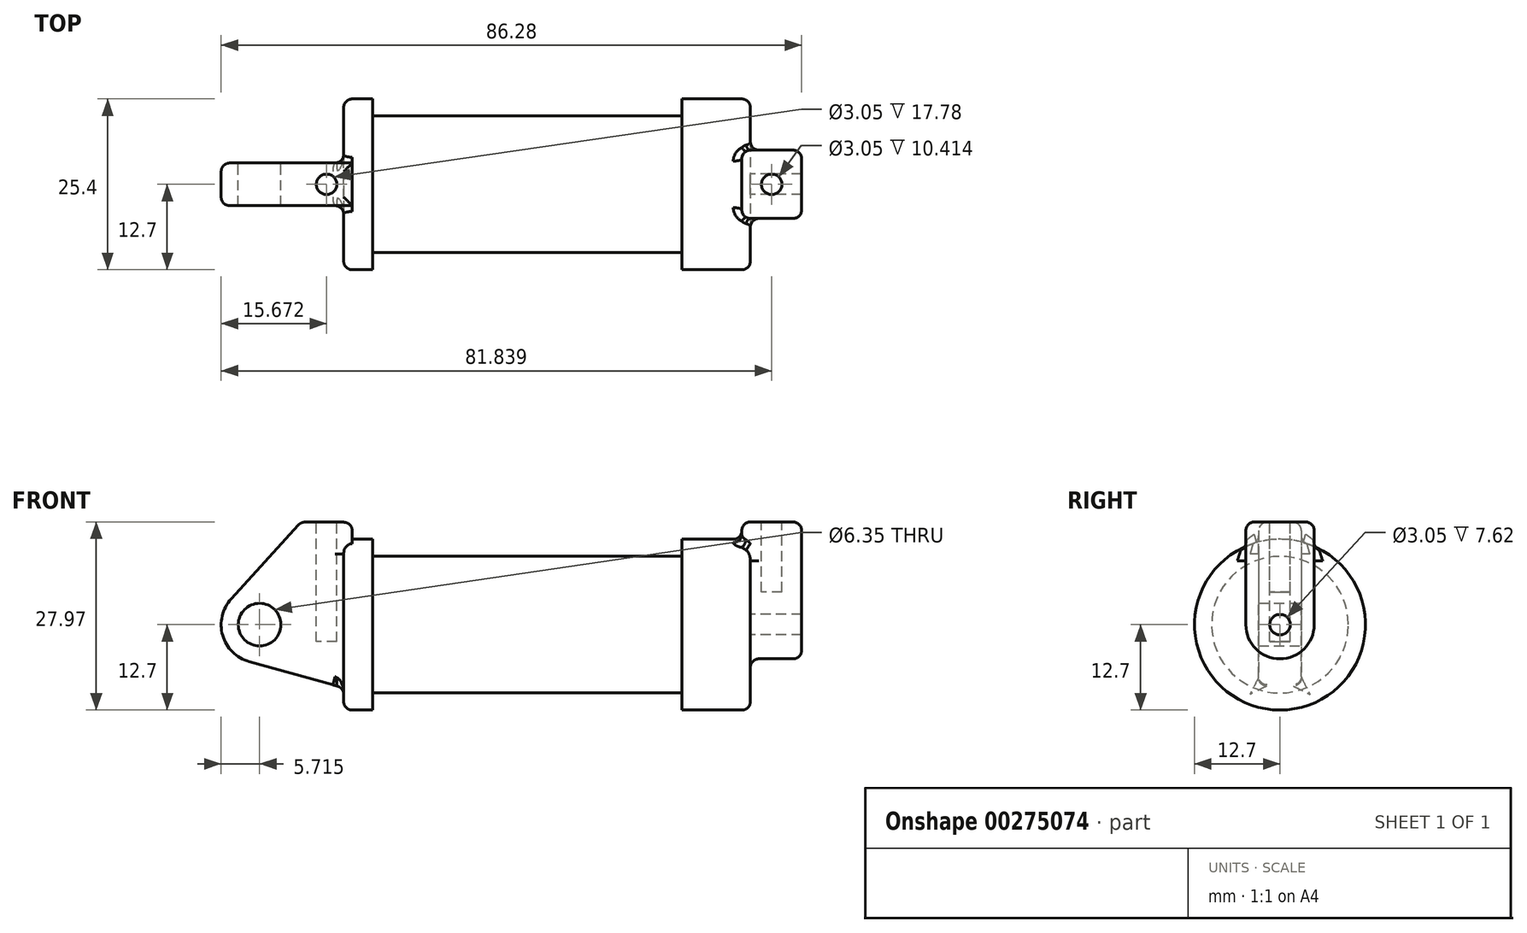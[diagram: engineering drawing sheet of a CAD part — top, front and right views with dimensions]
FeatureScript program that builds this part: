
annotation { "Feature Type Name" : "Feature", "Feature Type Description" : "" }
export const myFeature = defineFeature(function(context is Context, id is Id, definition is map)
    precondition{}
    {
        {
            var Q0;
            Q0=qCreatedBy(makeId("Front.planeOp"),FACE);
            var sketch = newSketch(context, id + "F0", { "sketchPlane" : qUnion([Q0])});
            skLineSegment(sketch, "E0", {"start": v(0, 0) * mm, "end": v(0, 12.7) * mm});
            skLineSegment(sketch, "E1", {"start": v(0, 12.7) * mm, "end": v(10.16, 12.7) * mm});
            skLineSegment(sketch, "E2", {"start": v(10.16, 12.7) * mm, "end": v(10.16, 10.16) * mm});
            skLineSegment(sketch, "E3", {"start": v(10.16, 10.16) * mm, "end": v(56.13, 10.16) * mm});
            skLineSegment(sketch, "E4", {"start": v(56.13, 10.16) * mm, "end": v(56.13, 12.7) * mm});
            skLineSegment(sketch, "E5", {"start": v(56.13, 12.7) * mm, "end": v(66.3, 12.7) * mm});
            skLineSegment(sketch, "E6", {"start": v(66.3, 12.7) * mm, "end": v(66.3, 0) * mm});
            skLineSegment(sketch, "E7", {"start": v(66.3, 0) * mm, "end": v(0, 0) * mm});
            skLineSegment(sketch, "E8", {"start": v(5.84, 15.24) * mm, "end": v(-0.5, 15.24) * mm});
            skLineSegment(sketch, "E9", {"start": v(-0.5, 15.24) * mm, "end": v(-10.88, 3.85) * mm});
            skLineSegment(sketch, "E10", {"start": v(0, 0) * mm, "end": v(-6.65, 0) * mm});
            skCircle(sketch, "E11", {"center": v(-6.65, 0) * mm, "radius": 5.72 * mm});
            skCircle(sketch, "E12", {"center": v(-6.65, 0) * mm, "radius": 3.18 * mm});
            skLineSegment(sketch, "E13", {"start": v(5.84, 15.24) * mm, "end": v(5.84, -9.4) * mm});
            skLineSegment(sketch, "E14", {"start": v(5.84, -9.4) * mm, "end": v(-8.18, -5.5) * mm});
            skSolve(sketch);
        }
        {
            var Q0;
            {var subQ0=sQuery(id+"F0.wireOp",EDGE,"E2");Q0=makeQuery(id+"F0.imprint","IMPRINT",FACE,{"disambiguationData":[TD([[makeQuery(id+"F0.imprint","IMPRINT",EDGE,{"derivedFrom":subQ0}),-1.0]])]});}
            var Q1;
            Q1=sQuery(id+"F0.wireOp",EDGE,"E7");
            revolve(context, id + "F1", {"entities" : qUnion([Q0]), "axis" : qUnion([Q1]), "revolveType" : RevolveType.FULL});
        }
        {
            var Q0;
            {var subQ3=sQuery(id+"F0.wireOp",EDGE,"E0");Q0=makeQuery(id+"F0.imprint","IMPRINT",FACE,{"disambiguationData":[TD([[makeQuery(id+"F0.imprint","IMPRINT",EDGE,{"derivedFrom":subQ3}),1.0]])]});}
            var Q1;
            {var subQ0=sQuery(id+"F0.wireOp",EDGE,"E0");Q1=makeQuery(id+"F0.imprint","IMPRINT",FACE,{"disambiguationData":[TD([[makeQuery(id+"F0.imprint","IMPRINT",EDGE,{"derivedFrom":subQ0}),-1.0]])]});}
            var Q2;
            {var subQ4=sQuery(id+"F0.wireOp",EDGE,"E12");Q2=makeQuery(id+"F0.imprint","IMPRINT",FACE,{"disambiguationData":[TD([[makeQuery(id+"F0.imprint","IMPRINT",EDGE,{"derivedFrom":subQ4}),-1.0]])]});}
            var Q3;
            {var subQ0=sQuery(id+"F0.wireOp",EDGE,"E14");Q3=makeQuery(id+"F0.imprint","IMPRINT",FACE,{"disambiguationData":[TD([[makeQuery(id+"F0.imprint","IMPRINT",EDGE,{"derivedFrom":subQ0}),-1.0]])]});}
            extrude(context, id + "F2", {"entities" : qUnion([Q0, Q1, Q2, Q3]), "operationType" : NewBodyOperationType.ADD, "endBound" : BoundingType.SYMMETRIC, "depth" : 6.35 * mm});
        }
        {
            var Q0;
            Q0=makeQuery(id+"F2.opExtrude","SWEPT_FACE",FACE,{"disambiguationData":[OSD([sQuery(id+"F0.wireOp",EDGE,"E13")])]});
            extrude(context, id + "F3", {"entities" : qUnion([Q0]), "operationType" : NewBodyOperationType.ADD, "depth" : 1.27 * mm});
        }
        {
            var Q0;
            Q0=makeQuery(id+"F1.opRevolve","SWEPT_FACE",FACE,{"disambiguationData":[OSD([sQuery(id+"F0.wireOp",EDGE,"E6")])]});
            var sketch = newSketch(context, id + "F4", { "sketchPlane" : qUnion([Q0])});
            skCircle(sketch, "E15", {"center": v(0, 0) * mm, "radius": 1.52 * mm});
            skCircle(sketch, "E16", {"center": v(0, 0) * mm, "radius": 5.08 * mm});
            skLineSegment(sketch, "E17", {"start": v(5.08, 0) * mm, "end": v(5.08, 15.27) * mm});
            skLineSegment(sketch, "E18", {"start": v(-5.08, 0) * mm, "end": v(-5.08, 15.27) * mm});
            skLineSegment(sketch, "E19", {"start": v(-5.08, 15.27) * mm, "end": v(5.08, 15.27) * mm});
            skSolve(sketch);
        }
        {
            var Q0;
            Q0=makeQuery(id+"F4.imprint","IMPRINT",FACE,{"disambiguationData":[TD([[makeQuery(id+"F4.imprint","IMPRINT",EDGE,{"derivedFrom":sQuery(id+"F4.wireOp",EDGE,"E15")}),-1.0]])]});
            var Q1;
            {var subQ0=sQuery(id+"F4.wireOp",EDGE,"E17");var subQ1=sQuery(id+"F4.wireOp",EDGE,"E16");var subQ2=makeQuery(id+"F4.imprint","INTERSECT",VERTEX,{"derivedFrom":[subQ1,subQ0]});Q1=makeQuery(id+"F4.imprint","IMPRINT",FACE,{"disambiguationData":[TD([[makeQuery(id+"F4.imprint","IMPRINT",EDGE,{"disambiguationData":[TD([[subQ2,-1.0]])],"derivedFrom":subQ1}),-1.0]])]});}
            var Q2;
            {var subQ0=sQuery(id+"F4.wireOp",EDGE,"E19");Q2=makeQuery(id+"F4.imprint","IMPRINT",FACE,{"disambiguationData":[TD([[makeQuery(id+"F4.imprint","IMPRINT",EDGE,{"derivedFrom":subQ0}),-1.0]])]});}
            var Q3;
            Q3=makeQuery(id+"F1.opRevolve","SWEPT_FACE",FACE,{"disambiguationData":[OSD([sQuery(id+"F0.wireOp",EDGE,"E2")])]});
            extrude(context, id + "F5", {"entities" : qUnion([Q0, Q1, Q2]), "operationType" : NewBodyOperationType.ADD, "endBoundEntityFace" : qUnion([Q3]), "depth" : 7.62 * mm});
        }
        {
            var Q0;
            Q0=makeQuery(id+"F5.opExtrude","CAP_FACE",FACE,{"disambiguationData":[OSD([sQuery(id+"F4.wireOp",EDGE,"E15"),sQuery(id+"F4.wireOp",EDGE,"E16"),sQuery(id+"F4.wireOp",EDGE,"E17"),sQuery(id+"F4.wireOp",EDGE,"E18"),sQuery(id+"F4.wireOp",EDGE,"E19")])],"isStart":true});
            extrude(context, id + "F6", {"entities" : qUnion([Q0]), "operationType" : NewBodyOperationType.ADD, "depth" : 1.27 * mm});
        }
        {
            var Q0;
            {var subQ0=sQuery(id+"F0.wireOp",EDGE,"E8");Q0=makeQuery(id+"F3.boolean.opBoolean","MERGE",FACE,{"derivedFrom":[makeQuery(id+"F2.opExtrude","SWEPT_FACE",FACE,{"disambiguationData":[OSD([subQ0])]}),makeQuery(id+"F3.opExtrude","SWEPT_FACE",FACE,{"disambiguationData":[OSD([subQ0,sQuery(id+"F0.wireOp",EDGE,"E13")])]})]});}
            var sketch = newSketch(context, id + "F7", { "sketchPlane" : qUnion([Q0])});
            skCircle(sketch, "E20", {"center": v(3.3, 0) * mm, "radius": 1.52 * mm});
            skSolve(sketch);
        }
        {
            var Q0;
            {var subQ0=sQuery(id+"F4.wireOp",EDGE,"E19");Q0=makeQuery(id+"F6.boolean.opBoolean","MERGE",FACE,{"derivedFrom":[makeQuery(id+"F5.opExtrude","SWEPT_FACE",FACE,{"disambiguationData":[OSD([subQ0])]}),makeQuery(id+"F6.opExtrude","SWEPT_FACE",FACE,{"disambiguationData":[OSD([subQ0])]})]});}
            var sketch = newSketch(context, id + "F8", { "sketchPlane" : qUnion([Q0])});
            skCircle(sketch, "E21", {"center": v(69.47, 0) * mm, "radius": 1.52 * mm});
            skSolve(sketch);
        }
        {
            var Q0;
            Q0=makeQuery(id+"F7.imprint","IMPRINT",FACE,{"disambiguationData":[TD([[makeQuery(id+"F7.imprint","IMPRINT",EDGE,{"derivedFrom":sQuery(id+"F7.wireOp",EDGE,"E20")}),1.0]])]});
            extrude(context, id + "F9", {"entities" : qUnion([Q0]), "operationType" : NewBodyOperationType.REMOVE, "oppositeDirection" : true, "depth" : 17.78 * mm});
        }
        {
            var Q0;
            Q0=makeQuery(id+"F8.imprint","IMPRINT",FACE,{"disambiguationData":[TD([[makeQuery(id+"F8.imprint","IMPRINT",EDGE,{"derivedFrom":sQuery(id+"F8.wireOp",EDGE,"E21")}),1.0]])]});
            extrude(context, id + "F10", {"entities" : qUnion([Q0]), "operationType" : NewBodyOperationType.REMOVE, "oppositeDirection" : true, "depth" : 10.4 * mm});
        }
        {
            var Q0;
            Q0=makeQuery(id+"F5.boolean.opBoolean","SPLIT",EDGE,{"disambiguationData":[OD(1.0)],"derivedFrom":makeQuery(id+"F1.opRevolve","SWEPT_EDGE",EDGE,{"disambiguationData":[OSD([sQuery(id+"F0.wireOp",EDGE,"E5"),sQuery(id+"F0.wireOp",EDGE,"E6")])]})});
            var Q1;
            Q1=makeQuery(id+"F1.opRevolve","SWEPT_FACE",FACE,{"disambiguationData":[OSD([sQuery(id+"F0.wireOp",EDGE,"E13")])]});
            fillet(context, id + "F11", {"entities" : qUnion([Q0, Q1]), "radius" : 1.27 * mm, "tangentPropagation" : true, "allowEdgeOverflow" : false});
        }
        {
            var Q0;
            Q0=makeQuery(id+"F2.opExtrude","SWEPT_FACE",FACE,{"disambiguationData":[OSD([sQuery(id+"F0.wireOp",EDGE,"E9")])]});
            var Q1;
            Q1=makeQuery(id+"F2.opExtrude","SWEPT_FACE",FACE,{"disambiguationData":[OSD([sQuery(id+"F0.wireOp",EDGE,"E11")])]});
            var Q2;
            Q2=makeQuery(id+"F2.opExtrude","SWEPT_FACE",FACE,{"disambiguationData":[OSD([sQuery(id+"F0.wireOp",EDGE,"E14")])]});
            var Q3;
            {var subQ0=sQuery(id+"F0.wireOp",EDGE,"E13");var subQ1=sQuery(id+"F0.wireOp",EDGE,"E8");Q3=makeQuery(id+"F3.boolean.opBoolean","MERGE",EDGE,{"derivedFrom":[makeQuery(id+"F2.opExtrude","CAP_EDGE",EDGE,{"disambiguationData":[OSD([subQ1])],"isStart":false}),makeQuery(id+"F3.opExtrude","SWEPT_EDGE",EDGE,{"disambiguationData":[OSD([subQ1,subQ0]),TDD([makeQuery(id+"F2.opExtrude","CAP_VERTEX",VERTEX,{"disambiguationData":[OSD([subQ1,subQ0])],"isStart":false})])]})]});}
            var Q4;
            Q4=makeQuery(id+"F3.opExtrude","CAP_EDGE",EDGE,{"disambiguationData":[OSD([sQuery(id+"F0.wireOp",EDGE,"E8"),sQuery(id+"F0.wireOp",EDGE,"E13")])],"isStart":false});
            var Q5;
            {var subQ0=sQuery(id+"F0.wireOp",EDGE,"E13");var subQ1=sQuery(id+"F0.wireOp",EDGE,"E8");Q5=makeQuery(id+"F3.boolean.opBoolean","MERGE",EDGE,{"derivedFrom":[makeQuery(id+"F2.opExtrude","CAP_EDGE",EDGE,{"disambiguationData":[OSD([subQ1])],"isStart":true}),makeQuery(id+"F3.opExtrude","SWEPT_EDGE",EDGE,{"disambiguationData":[OSD([subQ1,subQ0]),TDD([makeQuery(id+"F2.opExtrude","CAP_VERTEX",VERTEX,{"disambiguationData":[OSD([subQ1,subQ0])],"isStart":true})])]})]});}
            var Q6;
            {var subQ0=sQuery(id+"F0.wireOp",EDGE,"E14");var subQ1=sQuery(id+"F0.wireOp",EDGE,"E13");var subQ2=sQuery(id+"F0.wireOp",EDGE,"E12");var subQ3=sQuery(id+"F0.wireOp",EDGE,"E11");var subQ4=sQuery(id+"F0.wireOp",EDGE,"E9");var subQ5=sQuery(id+"F0.wireOp",EDGE,"E8");var subQ6=makeQuery(id+"F2.opExtrude","CAP_FACE",FACE,{"disambiguationData":[OSD([subQ5,subQ4,subQ3,subQ2,subQ1,subQ0])],"isStart":true});var subQ7=makeQuery(id+"F1.opRevolve","SWEPT_FACE",FACE,{"disambiguationData":[OSD([subQ1])]});var subQ8=sQuery(id+"F0.wireOp",EDGE,"E1");var subQ9=makeQuery(id+"F1.opRevolve","SWEPT_FACE",FACE,{"disambiguationData":[OSD([subQ8])]});var subQ10=makeQuery(id+"F2.opExtrude","SWEPT_FACE",FACE,{"disambiguationData":[OSD([subQ1])]});var subQ11=makeQuery(id+"F2.boolean.opBoolean","TWEAK_VERTEX",VERTEX,{"derivedFrom":[subQ9,subQ7,subQ6,subQ10]});Q6=makeQuery(id+"F11.opFillet","BLEND_EDGE",EDGE,{"blendedFrom":[makeQuery(id+"F3.boolean.opBoolean","MERGE",VERTEX,{"derivedFrom":[subQ11,makeQuery(id+"F3.opExtrude","CAP_VERTEX",VERTEX,{"disambiguationData":[OSD([subQ8,subQ5,subQ4,subQ3,subQ2,subQ1,subQ0]),TDD([subQ11])],"isStart":true})]}),makeQuery(id+"F3.boolean.opBoolean","MERGE",FACE,{"derivedFrom":[subQ6,makeQuery(id+"F3.opExtrude","SWEPT_FACE",FACE,{"disambiguationData":[OSD([subQ1]),TDD([makeQuery(id+"F2.boolean.opBoolean","SPLIT",EDGE,{"disambiguationData":[TD([makeQuery(id+"F2.opExtrude","SWEPT_FACE",FACE,{"disambiguationData":[OSD([subQ5])]})])],"derivedFrom":makeQuery(id+"F2.opExtrude","CAP_EDGE",EDGE,{"disambiguationData":[OSD([subQ1])],"isStart":true})})])]})]})],"blendedInto":[makeQuery(id+"F3.boolean.opBoolean","MERGE",FACE,{"derivedFrom":[subQ6,makeQuery(id+"F3.opExtrude","SWEPT_FACE",FACE,{"disambiguationData":[OSD([subQ1]),TDD([makeQuery(id+"F2.boolean.opBoolean","SPLIT",EDGE,{"disambiguationData":[TD([makeQuery(id+"F2.opExtrude","SWEPT_FACE",FACE,{"disambiguationData":[OSD([subQ5])]})])],"derivedFrom":makeQuery(id+"F2.opExtrude","CAP_EDGE",EDGE,{"disambiguationData":[OSD([subQ1])],"isStart":true})})])]})]})]});}
            var Q7;
            {var subQ0=sQuery(id+"F0.wireOp",EDGE,"E8");var subQ1=sQuery(id+"F0.wireOp",EDGE,"E14");var subQ2=sQuery(id+"F0.wireOp",EDGE,"E13");var subQ3=sQuery(id+"F0.wireOp",EDGE,"E12");var subQ4=sQuery(id+"F0.wireOp",EDGE,"E11");var subQ5=sQuery(id+"F0.wireOp",EDGE,"E9");var subQ6=makeQuery(id+"F2.opExtrude","CAP_FACE",FACE,{"disambiguationData":[OSD([subQ0,subQ5,subQ4,subQ3,subQ2,subQ1])],"isStart":false});var subQ7=makeQuery(id+"F1.opRevolve","SWEPT_FACE",FACE,{"disambiguationData":[OSD([subQ2])]});var subQ8=sQuery(id+"F0.wireOp",EDGE,"E1");var subQ9=makeQuery(id+"F1.opRevolve","SWEPT_FACE",FACE,{"disambiguationData":[OSD([subQ8])]});var subQ10=makeQuery(id+"F2.opExtrude","SWEPT_FACE",FACE,{"disambiguationData":[OSD([subQ2])]});var subQ11=makeQuery(id+"F2.boolean.opBoolean","TWEAK_VERTEX",VERTEX,{"derivedFrom":[subQ9,subQ7,subQ6,subQ10]});Q7=makeQuery(id+"F11.opFillet","BLEND_EDGE",EDGE,{"blendedFrom":[makeQuery(id+"F3.boolean.opBoolean","MERGE",VERTEX,{"derivedFrom":[subQ11,makeQuery(id+"F3.opExtrude","CAP_VERTEX",VERTEX,{"disambiguationData":[OSD([subQ8,subQ0,subQ5,subQ4,subQ3,subQ2,subQ1]),TDD([subQ11])],"isStart":true})]}),makeQuery(id+"F3.boolean.opBoolean","MERGE",FACE,{"derivedFrom":[subQ6,makeQuery(id+"F3.opExtrude","SWEPT_FACE",FACE,{"disambiguationData":[OSD([subQ2]),TDD([makeQuery(id+"F2.boolean.opBoolean","SPLIT",EDGE,{"disambiguationData":[TD([makeQuery(id+"F2.opExtrude","SWEPT_FACE",FACE,{"disambiguationData":[OSD([subQ0])]})])],"derivedFrom":makeQuery(id+"F2.opExtrude","CAP_EDGE",EDGE,{"disambiguationData":[OSD([subQ2])],"isStart":false})})])]})]})],"blendedInto":[makeQuery(id+"F3.boolean.opBoolean","MERGE",FACE,{"derivedFrom":[subQ6,makeQuery(id+"F3.opExtrude","SWEPT_FACE",FACE,{"disambiguationData":[OSD([subQ2]),TDD([makeQuery(id+"F2.boolean.opBoolean","SPLIT",EDGE,{"disambiguationData":[TD([makeQuery(id+"F2.opExtrude","SWEPT_FACE",FACE,{"disambiguationData":[OSD([subQ0])]})])],"derivedFrom":makeQuery(id+"F2.opExtrude","CAP_EDGE",EDGE,{"disambiguationData":[OSD([subQ2])],"isStart":false})})])]})]})]});}
            var Q8;
            {var subQ0=sQuery(id+"F0.wireOp",EDGE,"E8");var subQ1=sQuery(id+"F0.wireOp",EDGE,"E14");var subQ2=sQuery(id+"F0.wireOp",EDGE,"E13");var subQ3=makeQuery(id+"F2.opExtrude","CAP_FACE",FACE,{"disambiguationData":[OSD([subQ0,sQuery(id+"F0.wireOp",EDGE,"E9"),sQuery(id+"F0.wireOp",EDGE,"E11"),sQuery(id+"F0.wireOp",EDGE,"E12"),subQ2,subQ1])],"isStart":false});var subQ7=makeQuery(id+"F2.opExtrude","CAP_EDGE",EDGE,{"disambiguationData":[OSD([subQ2])],"isStart":false});Q8=makeQuery(id+"F11.opFillet","BLEND_EDGE",EDGE,{"blendedFrom":[makeQuery(id+"F2.boolean.opBoolean","SPLIT",EDGE,{"disambiguationData":[TD([makeQuery(id+"F2.opExtrude","SWEPT_FACE",FACE,{"disambiguationData":[OSD([subQ1])]})])],"derivedFrom":subQ7}),makeQuery(id+"F3.boolean.opBoolean","MERGE",FACE,{"derivedFrom":[subQ3,makeQuery(id+"F3.opExtrude","SWEPT_FACE",FACE,{"disambiguationData":[OSD([subQ2]),TDD([makeQuery(id+"F2.boolean.opBoolean","SPLIT",EDGE,{"disambiguationData":[TD([makeQuery(id+"F2.opExtrude","SWEPT_FACE",FACE,{"disambiguationData":[OSD([subQ0])]})])],"derivedFrom":subQ7})])]})]})],"blendedInto":[makeQuery(id+"F3.boolean.opBoolean","MERGE",FACE,{"derivedFrom":[subQ3,makeQuery(id+"F3.opExtrude","SWEPT_FACE",FACE,{"disambiguationData":[OSD([subQ2]),TDD([makeQuery(id+"F2.boolean.opBoolean","SPLIT",EDGE,{"disambiguationData":[TD([makeQuery(id+"F2.opExtrude","SWEPT_FACE",FACE,{"disambiguationData":[OSD([subQ0])]})])],"derivedFrom":subQ7})])]})]})]});}
            var Q9;
            {var subQ0=sQuery(id+"F0.wireOp",EDGE,"E13");var subQ1=sQuery(id+"F0.wireOp",EDGE,"E14");Q9=makeQuery(id+"F11.opFillet","BLEND_EDGE",EDGE,{"blendedFrom":[makeQuery(id+"F2.opExtrude","SWEPT_EDGE",EDGE,{"disambiguationData":[OSD([subQ0,subQ1])]}),makeQuery(id+"F2.boolean.opBoolean","SPLIT",EDGE,{"disambiguationData":[TD([makeQuery(id+"F2.opExtrude","SWEPT_FACE",FACE,{"disambiguationData":[OSD([subQ1])]})])],"derivedFrom":makeQuery(id+"F2.opExtrude","CAP_EDGE",EDGE,{"disambiguationData":[OSD([subQ0])],"isStart":true})})],"blendedInto":[]});}
            var Q10;
            {var subQ0=sQuery(id+"F0.wireOp",EDGE,"E13");Q10=makeQuery(id+"F11.opFillet","BLEND_EDGE",EDGE,{"blendedFrom":[makeQuery(id+"F2.opExtrude","SWEPT_EDGE",EDGE,{"disambiguationData":[OSD([subQ0,sQuery(id+"F0.wireOp",EDGE,"E14")])]}),makeQuery(id+"F1.opRevolve","SWEPT_FACE",FACE,{"disambiguationData":[OSD([subQ0])]})],"blendedInto":[makeQuery(id+"F1.opRevolve","SWEPT_FACE",FACE,{"disambiguationData":[OSD([subQ0])]})]});}
            fillet(context, id + "F12", {"entities" : qUnion([Q0, Q1, Q2, Q3, Q4, Q5, Q6, Q7, Q8, Q9, Q10]), "radius" : 1.27 * mm, "tangentPropagation" : true, "allowEdgeOverflow" : false});
        }
        {
            var Q0;
            Q0=makeQuery(id+"F5.opExtrude","CAP_EDGE",EDGE,{"disambiguationData":[OSD([sQuery(id+"F4.wireOp",EDGE,"E19")])],"isStart":false});
            var Q1;
            {var subQ0=sQuery(id+"F4.wireOp",EDGE,"E19");var subQ1=sQuery(id+"F4.wireOp",EDGE,"E18");Q1=makeQuery(id+"F6.boolean.opBoolean","MERGE",EDGE,{"derivedFrom":[makeQuery(id+"F5.opExtrude","SWEPT_EDGE",EDGE,{"disambiguationData":[OSD([subQ1,subQ0])]}),makeQuery(id+"F6.opExtrude","SWEPT_EDGE",EDGE,{"disambiguationData":[OSD([subQ1,subQ0])]})]});}
            var Q2;
            Q2=makeQuery(id+"F6.opExtrude","CAP_EDGE",EDGE,{"disambiguationData":[OSD([sQuery(id+"F4.wireOp",EDGE,"E19")])],"isStart":false});
            var Q3;
            {var subQ0=sQuery(id+"F4.wireOp",EDGE,"E19");var subQ1=sQuery(id+"F4.wireOp",EDGE,"E17");Q3=makeQuery(id+"F6.boolean.opBoolean","MERGE",EDGE,{"derivedFrom":[makeQuery(id+"F5.opExtrude","SWEPT_EDGE",EDGE,{"disambiguationData":[OSD([subQ1,subQ0])]}),makeQuery(id+"F6.opExtrude","SWEPT_EDGE",EDGE,{"disambiguationData":[OSD([subQ1,subQ0])]})]});}
            var Q4;
            Q4=makeQuery(id+"F5.opExtrude","SWEPT_FACE",FACE,{"disambiguationData":[OSD([sQuery(id+"F4.wireOp",EDGE,"E16")])]});
            var Q5;
            Q5=makeQuery(id+"F6.opExtrude","CAP_FACE",FACE,{"disambiguationData":[OSD([sQuery(id+"F4.wireOp",EDGE,"E15"),sQuery(id+"F4.wireOp",EDGE,"E16"),sQuery(id+"F4.wireOp",EDGE,"E17"),sQuery(id+"F4.wireOp",EDGE,"E18"),sQuery(id+"F4.wireOp",EDGE,"E19")])],"isStart":false});
            fillet(context, id + "F13", {"entities" : qUnion([Q0, Q1, Q2, Q3, Q4, Q5]), "radius" : 1.27 * mm, "tangentPropagation" : true, "allowEdgeOverflow" : false});
        }
    });
